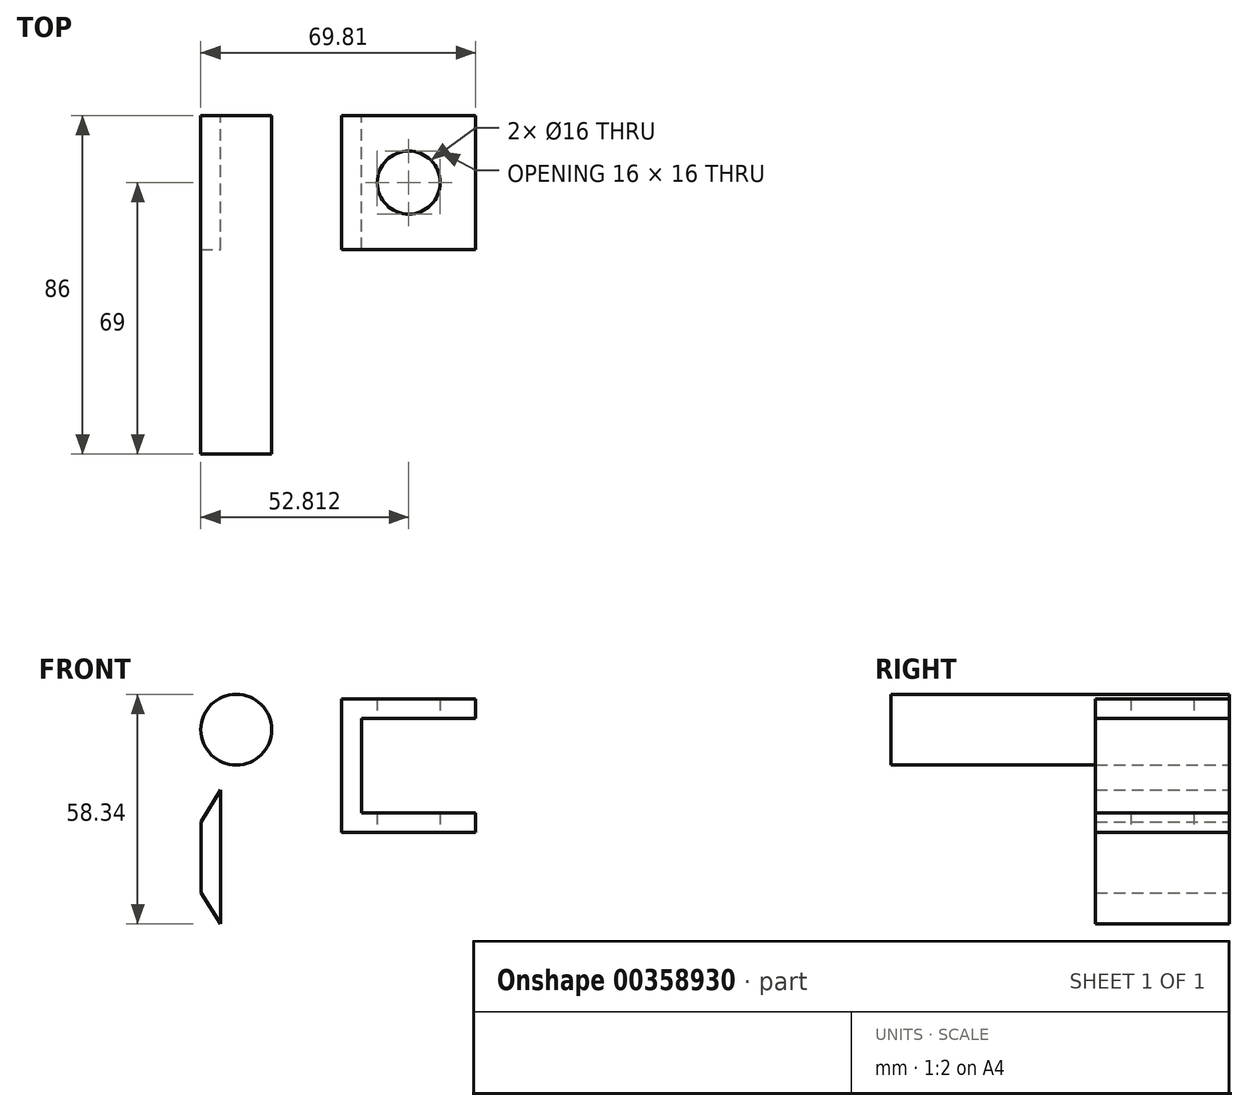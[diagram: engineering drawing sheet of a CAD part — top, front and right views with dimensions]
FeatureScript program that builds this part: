
annotation { "Feature Type Name" : "Feature", "Feature Type Description" : "" }
export const myFeature = defineFeature(function(context is Context, id is Id, definition is map)
    precondition{}
    {
        {
            var Q0;
            Q0=qCreatedBy(makeId("Front.planeOp"),FACE);
            var sketch = newSketch(context, id + "F0", { "sketchPlane" : qUnion([Q0])});
            skCircle(sketch, "E0", {"center": v(-62.17, 33.75) * mm, "radius": 9 * mm});
            skSolve(sketch);
        }
        {
            var Q0;
            Q0 = qSketchRegion(id + "F0", true);
            extrude(context, id + "F1", {"entities" : qUnion([Q0]), "depth" : 86 * mm});
        }
        {
            var Q0;
            Q0=qCreatedBy(makeId("Front.planeOp"),FACE);
            var sketch = newSketch(context, id + "F2", { "sketchPlane" : qUnion([Q0])});
            skLineSegment(sketch, "E1", {"start": v(-35.36, 41.62) * mm, "end": v(-1.36, 41.62) * mm});
            skLineSegment(sketch, "E2", {"start": v(-1.36, 41.62) * mm, "end": v(-1.36, 36.62) * mm});
            skLineSegment(sketch, "E3", {"start": v(-1.36, 36.62) * mm, "end": v(-30.36, 36.62) * mm});
            skLineSegment(sketch, "E4", {"start": v(-30.36, 36.62) * mm, "end": v(-30.36, 12.62) * mm});
            skLineSegment(sketch, "E5", {"start": v(-30.36, 12.62) * mm, "end": v(-1.36, 12.62) * mm});
            skLineSegment(sketch, "E6", {"start": v(-1.36, 12.62) * mm, "end": v(-1.36, 7.62) * mm});
            skLineSegment(sketch, "E7", {"start": v(-1.36, 7.62) * mm, "end": v(-35.36, 7.62) * mm});
            skLineSegment(sketch, "E8", {"start": v(-35.36, 7.62) * mm, "end": v(-35.36, 41.62) * mm});
            skLineSegment(sketch, "E9", {"start": v(-66.16, 18.41) * mm, "end": v(-66.16, -15.59) * mm});
            skPoint(sketch, "E10", {"position": v(-71.16, 10.27) * mm});
            skPoint(sketch, "E11", {"position": v(-71.16, -7.73) * mm});
            skLineSegment(sketch, "E12", {"start": v(-71.16, 10.27) * mm, "end": v(-71.16, -7.73) * mm});
            skLineSegment(sketch, "E13", {"start": v(-71.16, 10.27) * mm, "end": v(-66.16, 18.41) * mm});
            skLineSegment(sketch, "E14", {"start": v(-66.16, -15.59) * mm, "end": v(-71.16, -7.73) * mm});
            skSolve(sketch);
        }
        {
            var Q0;
            Q0 = qSketchRegion(id + "F2", true);
            extrude(context, id + "F3", {"entities" : qUnion([Q0]), "depth" : 34 * mm});
        }
        {
            var Q0;
            Q0=makeQuery(id+"F3.opExtrude","SWEPT_FACE",FACE,{"disambiguationData":[OSD([sQuery(id+"F2.wireOp",EDGE,"E7")])]});
            var sketch = newSketch(context, id + "F4", { "sketchPlane" : qUnion([Q0])});
            skCircle(sketch, "E15", {"center": v(-18.36, 17) * mm, "radius": 8 * mm});
            skArc(sketch, "E16", {"start": v(-18.36, 0) * mm, "mid": v(-1.36, 17) * mm, "end": v(-18.36, 34) * mm});
            skSolve(sketch);
        }
        {
            var Q0;
            Q0=sQuery(id+"F4.wireOp",VERTEX,"E15.center");
            var Q1;
            Q1=makeQuery(id+"F3.opExtrude","SWEPT_BODY",BODY,{"disambiguationData":[OSD([sQuery(id+"F2.wireOp",EDGE,"E1"),sQuery(id+"F2.wireOp",EDGE,"E2"),sQuery(id+"F2.wireOp",EDGE,"E3"),sQuery(id+"F2.wireOp",EDGE,"E4"),sQuery(id+"F2.wireOp",EDGE,"E5"),sQuery(id+"F2.wireOp",EDGE,"E6"),sQuery(id+"F2.wireOp",EDGE,"E7"),sQuery(id+"F2.wireOp",EDGE,"E8")])]});
            hole(context, id + "F5", {"style" : HoleStyle.SIMPLE, "endStyle" : HoleEndStyle.THROUGH, "holeDiameter" : 16 * mm, "isTappedThrough" : true, "tappedDepth" : 12 * mm, "tapClearance" : 3, "locations" : qUnion([Q0]), "scope" : qUnion([Q1])});
        }
    });
